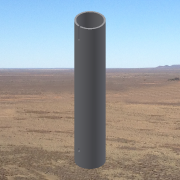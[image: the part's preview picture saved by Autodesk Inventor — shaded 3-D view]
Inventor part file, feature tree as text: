
AUTODESK INVENTOR PART (.ipt)
format: ipt  version: 2014 SP1 (Build 180222100, 222)  size: 158,720 bytes
history: native  units: in
note: dims shown in document units (in); Inventor stores cm internally (conversion verified against a paired STEP export)
features: extrude x4, sketch x4, plane x1
ambient origin geometry x8: Origin, YZ Plane, XZ Plane, XY Plane, X Axis, Y Axis, Z Axis, Center Point
bodies: Solid1 (feature_tree)
feature tree (9):
  extrude  "Extrusion1"  Depth=0.216in
  plane  "Work Plane1"
  extrude  "Extrusion2"  Depth=1.75in
  extrude  "Extrusion3"  Depth=1.75in
  extrude  "Extrusion4"  Depth=0.25in
  sketch  "Sketch1"  dims[d0=3.5in d1=0.216in]
  sketch  "Sketch2"  dims[d2=18.95in d3=0.0in d4=1.75in]
  sketch  "Sketch4"  dims[d5=1.75in d6=0.2in]
  sketch  "Sketch5"  dims[d7=1.0in d8=0.0in d18=0.25in d19=0.25in d20=2.13in d21=1.0in d22=0.0in d23=0.88in d24=0.25in d25=0.0in]
